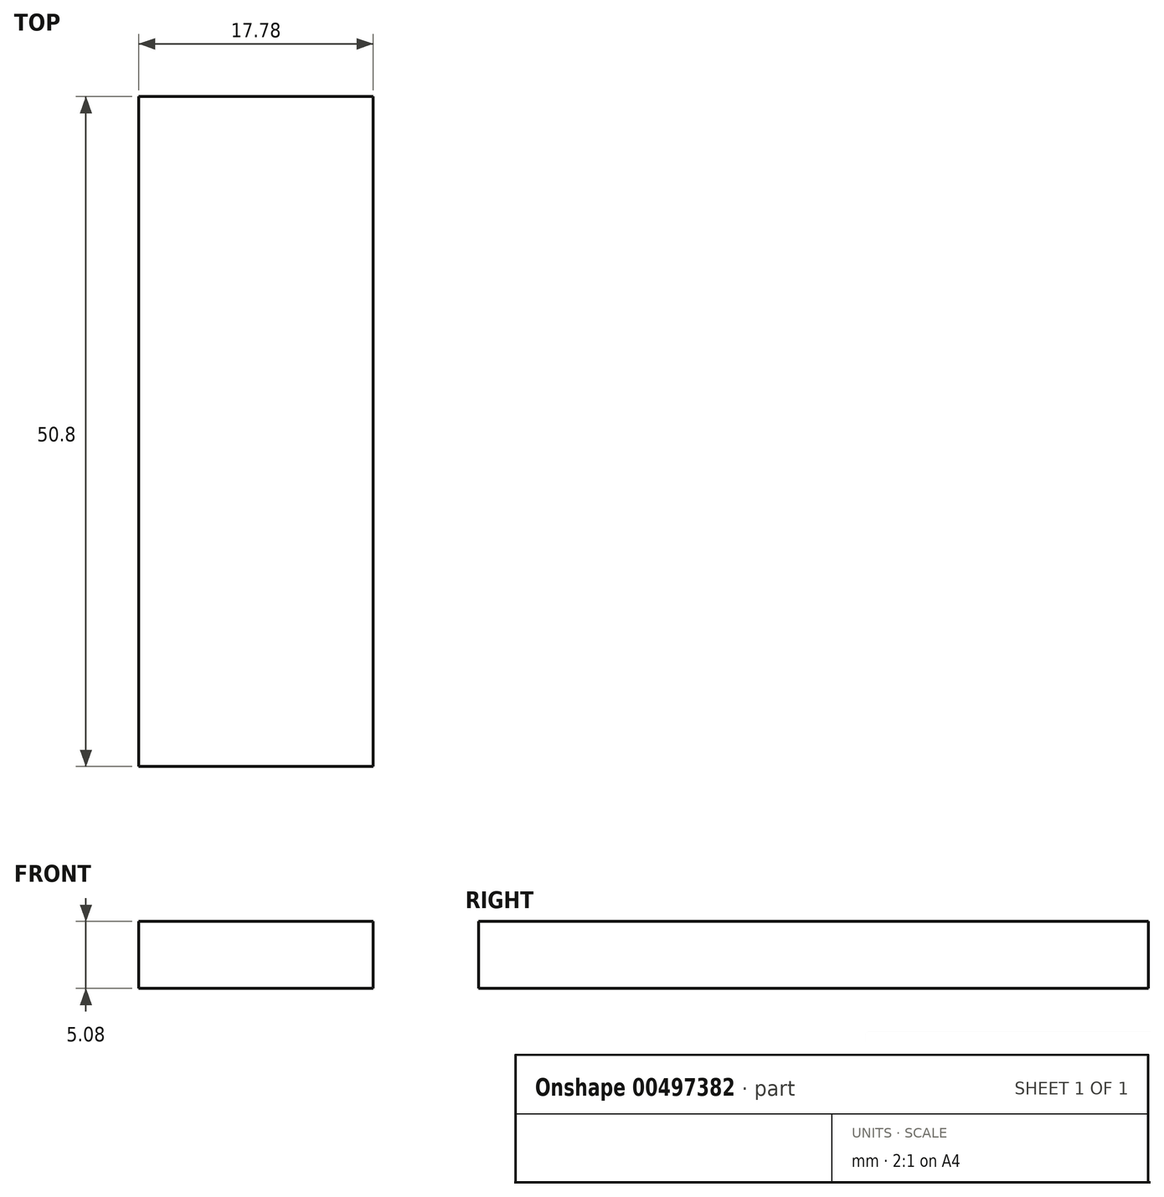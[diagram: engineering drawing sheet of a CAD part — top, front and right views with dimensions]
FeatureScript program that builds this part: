
annotation { "Feature Type Name" : "Feature", "Feature Type Description" : "" }
export const myFeature = defineFeature(function(context is Context, id is Id, definition is map)
    precondition{}
    {
        {
            var Q0;
            Q0=qCreatedBy(makeId("Top.planeOp"),FACE);
            var sketch = newSketch(context, id + "F0", { "sketchPlane" : qUnion([Q0])});
            skLineSegment(sketch, "E0.bottom", {"start": v(8.89, 0) * mm, "end": v(-8.89, 0) * mm});
            skLineSegment(sketch, "E0.top", {"start": v(8.89, 50.8) * mm, "end": v(-8.9, 50.8) * mm});
            skLineSegment(sketch, "E0.left", {"start": v(8.9, 0) * mm, "end": v(8.89, 50.8) * mm});
            skLineSegment(sketch, "E0.right", {"start": v(-8.89, 0) * mm, "end": v(-8.9, 50.8) * mm});
            skPoint(sketch, "E1", {"position": v(0, 0) * mm});
            skPoint(sketch, "E2", {"position": v(8.89, 25.4) * mm});
            skSolve(sketch);
        }
        {
            var Q0;
            Q0 = qSketchRegion(id + "F0", true);
            extrude(context, id + "F1", {"entities" : qUnion([Q0]), "oppositeDirection" : true, "depth" : 5.08 * mm});
        }
    });
